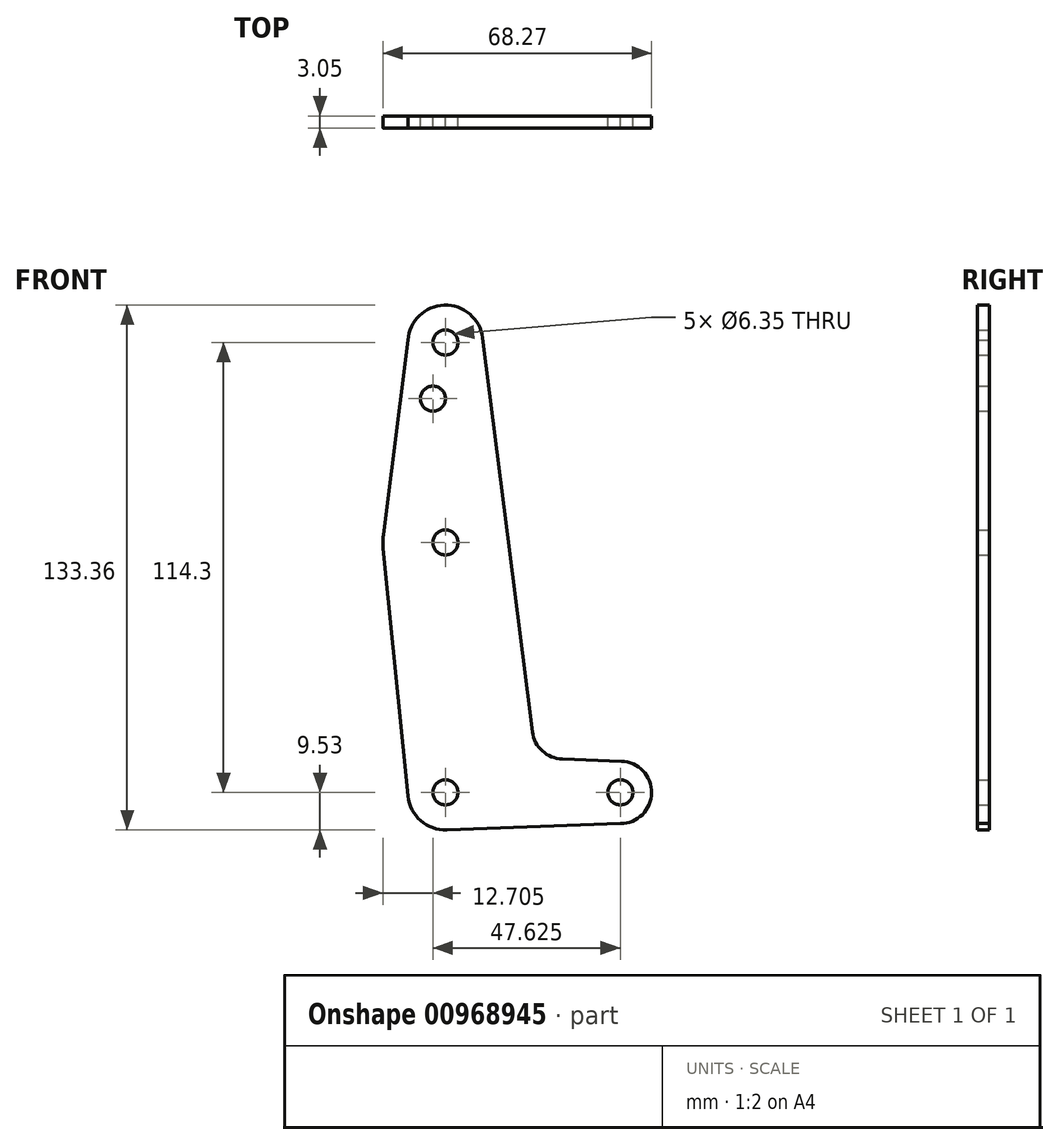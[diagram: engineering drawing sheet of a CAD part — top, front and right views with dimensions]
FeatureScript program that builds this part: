
annotation { "Feature Type Name" : "Feature", "Feature Type Description" : "" }
export const myFeature = defineFeature(function(context is Context, id is Id, definition is map)
    precondition{}
    {
        {
            var Q0;
            Q0=qCreatedBy(makeId("Front.planeOp"),FACE);
            var sketch = newSketch(context, id + "F0", { "sketchPlane" : qUnion([Q0])});
            skLineSegment(sketch, "E0", {"start": v(0, 114.3) * mm, "end": v(0, 0) * mm, "construction": true});
            skCircle(sketch, "E1", {"center": v(0, 114.3) * mm, "radius": 9.53 * mm});
            skCircle(sketch, "E2", {"center": v(0, 0) * mm, "radius": 9.53 * mm});
            skCircle(sketch, "E3", {"center": v(0, 63.5) * mm, "radius": 15.88 * mm});
            skLineSegment(sketch, "E4", {"start": v(0, 0) * mm, "end": v(44.45, 0) * mm, "construction": true});
            skCircle(sketch, "E5", {"center": v(44.45, 0) * mm, "radius": 7.94 * mm});
            skLineSegment(sketch, "E6", {"start": v(-9.5, 114.88) * mm, "end": v(-15.75, 65.5) * mm});
            skLineSegment(sketch, "E7", {"start": v(-15.75, 65.5) * mm, "end": v(-15.1, 58.6) * mm});
            skLineSegment(sketch, "E8", {"start": v(22.1, 15.41) * mm, "end": v(15.75, 65.5) * mm});
            skLineSegment(sketch, "E9", {"start": v(15.75, 65.5) * mm, "end": v(9.45, 115.5) * mm});
            skLineSegment(sketch, "E10", {"start": v(29.7, 8.47) * mm, "end": v(44.73, 7.93) * mm});
            skLineSegment(sketch, "E11", {"start": v(44.45, -7.94) * mm, "end": v(0, -9.53) * mm});
            skCircle(sketch, "E12", {"center": v(0, 114.3) * mm, "radius": 3.18 * mm});
            skCircle(sketch, "E13", {"center": v(0, 63.5) * mm, "radius": 3.18 * mm});
            skCircle(sketch, "E14", {"center": v(-3.18, 100.03) * mm, "radius": 3.18 * mm});
            skCircle(sketch, "E15", {"center": v(0, 0) * mm, "radius": 3.18 * mm});
            skCircle(sketch, "E16", {"center": v(44.45, 0) * mm, "radius": 3.18 * mm});
            skArc(sketch, "E17.filletArc", {"start": v(22.1, 15.41) * mm, "mid": v(24.62, 10.54) * mm, "end": v(29.7, 8.47) * mm});
            skPoint(sketch, "E18.orphan", {"position": v(-9.57, 0) * mm});
            skLineSegment(sketch, "E19", {"start": v(112.34, -101.59) * mm, "end": v(112.34, -112.13) * mm});
            skLineSegment(sketch, "E20", {"start": v(-9.48, -0.95) * mm, "end": v(-15.8, 61.91) * mm});
            skSolve(sketch);
        }
        {
            var Q0;
            Q0 = qSketchRegion(id + "F0", true);
            extrude(context, id + "F1", {"entities" : qUnion([Q0]), "depth" : 3.05 * mm, "offsetDistance" : 25.4 * mm});
        }
    });
